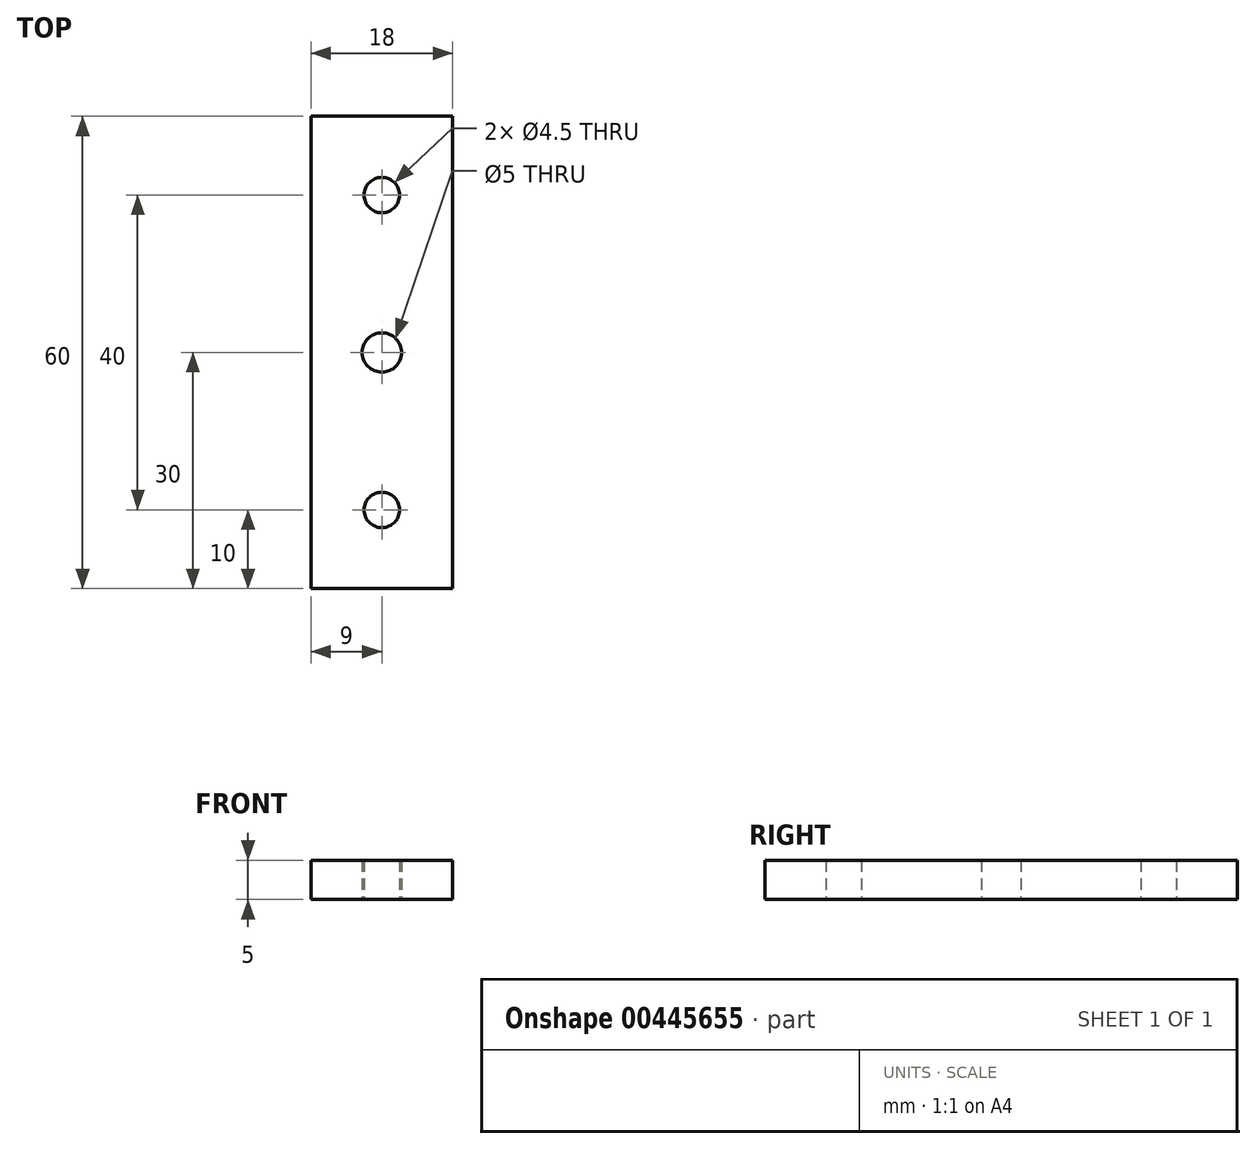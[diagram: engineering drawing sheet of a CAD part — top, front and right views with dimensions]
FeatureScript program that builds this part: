
annotation { "Feature Type Name" : "Feature", "Feature Type Description" : "" }
export const myFeature = defineFeature(function(context is Context, id is Id, definition is map)
    precondition{}
    {
        {
            var Q0;
            Q0=qCreatedBy(makeId("Top.planeOp"),FACE);
            var sketch = newSketch(context, id + "F0", { "sketchPlane" : qUnion([Q0])});
            skLineSegment(sketch, "E0.bottom", {"start": v(-9, -30) * mm, "end": v(9, -30) * mm});
            skLineSegment(sketch, "E0.top", {"start": v(-9, 30) * mm, "end": v(9, 30) * mm});
            skLineSegment(sketch, "E0.left", {"start": v(-9, -30) * mm, "end": v(-9, 30) * mm});
            skLineSegment(sketch, "E0.right", {"start": v(9, -30) * mm, "end": v(9, 30) * mm});
            skPoint(sketch, "E0.middle", {"position": v(0, 0) * mm});
            skCircle(sketch, "E1", {"center": v(0, 0) * mm, "radius": 2.5 * mm});
            skCircle(sketch, "E2", {"center": v(0, 20) * mm, "radius": 2.25 * mm});
            skCircle(sketch, "E3.MirrorC", {"center": v(0, -20) * mm, "radius": 2.25 * mm});
            skSolve(sketch);
        }
        {
            var Q0;
            Q0=qSketchRegion(id+"F0",true);
            extrude(context, id + "F1", {"entities" : qUnion([Q0]), "depth" : 5 * mm});
        }
    });
